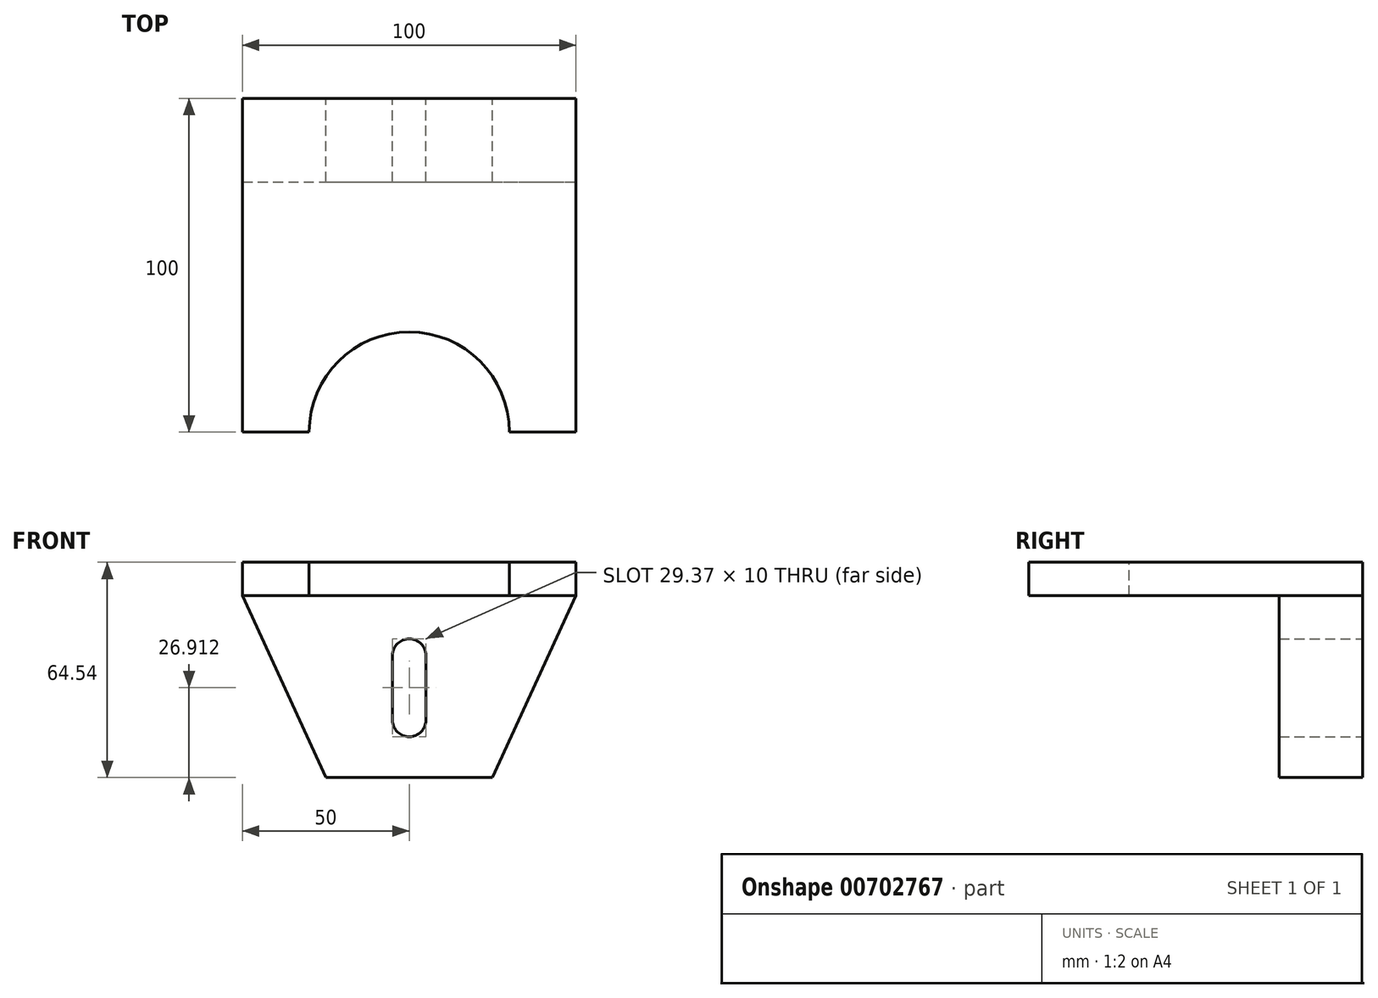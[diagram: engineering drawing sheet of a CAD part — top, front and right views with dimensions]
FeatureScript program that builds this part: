
annotation { "Feature Type Name" : "Feature", "Feature Type Description" : "" }
export const myFeature = defineFeature(function(context is Context, id is Id, definition is map)
    precondition{}
    {
        {
            var Q0;
            Q0=qCreatedBy(makeId("Front.planeOp"),FACE);
            var sketch = newSketch(context, id + "F0", { "sketchPlane" : qUnion([Q0])});
            skLineSegment(sketch, "E0", {"start": v(0, 0) * mm, "end": v(50, 0) * mm});
            skLineSegment(sketch, "E1", {"start": v(50, 0) * mm, "end": v(75, 54.54) * mm});
            skLineSegment(sketch, "E2", {"start": v(75, 54.54) * mm, "end": v(75, 64.54) * mm});
            skLineSegment(sketch, "E3", {"start": v(75, 64.54) * mm, "end": v(-25, 64.54) * mm});
            skLineSegment(sketch, "E4", {"start": v(-25, 64.54) * mm, "end": v(-25, 54.54) * mm});
            skLineSegment(sketch, "E5", {"start": v(-25, 54.54) * mm, "end": v(0, 0) * mm});
            skLineSegment(sketch, "E6", {"start": v(-25, 54.54) * mm, "end": v(75, 54.54) * mm});
            skSolve(sketch);
        }
        {
            var Q0;
            Q0=makeQuery(id+"F0.imprint","IMPRINT",FACE,{"disambiguationData":[TD([[makeQuery(id+"F0.imprint","IMPRINT",EDGE,{"derivedFrom":sQuery(id+"F0.wireOp",EDGE,"E2")}),1.0]])]});
            extrude(context, id + "F1", {"entities" : qUnion([Q0]), "depth" : 100 * mm, "offsetDistance" : 25 * mm});
        }
        {
            var Q0;
            Q0=makeQuery(id+"F0.imprint","IMPRINT",FACE,{"disambiguationData":[TD([[makeQuery(id+"F0.imprint","IMPRINT",EDGE,{"derivedFrom":sQuery(id+"F0.wireOp",EDGE,"E0")}),1.0]])]});
            extrude(context, id + "F2", {"entities" : qUnion([Q0]), "operationType" : NewBodyOperationType.ADD, "depth" : 25 * mm, "offsetDistance" : 25 * mm});
        }
        {
            var Q0;
            {var subQ0=sQuery(id+"F0.wireOp",EDGE,"E6");Q0=makeQuery(id+"F2.boolean.opBoolean","MERGE",FACE,{"derivedFrom":[makeQuery(id+"F1.opExtrude","CAP_FACE",FACE,{"disambiguationData":[OSD([sQuery(id+"F0.wireOp",EDGE,"E2"),sQuery(id+"F0.wireOp",EDGE,"E3"),sQuery(id+"F0.wireOp",EDGE,"E4"),subQ0])],"isStart":true}),makeQuery(id+"F2.opExtrude","CAP_FACE",FACE,{"disambiguationData":[OSD([sQuery(id+"F0.wireOp",EDGE,"E0"),sQuery(id+"F0.wireOp",EDGE,"E1"),sQuery(id+"F0.wireOp",EDGE,"E5"),subQ0])],"isStart":true})]});}
            var sketch = newSketch(context, id + "F3", { "sketchPlane" : qUnion([Q0])});
            skArc(sketch, "E7", {"start": v(-20, 36.6) * mm, "mid": v(-25, 41.6) * mm, "end": v(-30, 36.6) * mm});
            skPoint(sketch, "E7.centerSnap0", {"position": v(-25, 64.54) * mm});
            skArc(sketch, "E8", {"start": v(-30, 17.23) * mm, "mid": v(-25, 12.23) * mm, "end": v(-20, 17.23) * mm});
            skLineSegment(sketch, "E9", {"start": v(-30, 36.6) * mm, "end": v(-30, 17.23) * mm});
            skLineSegment(sketch, "E10", {"start": v(-20, 36.6) * mm, "end": v(-20, 17.23) * mm});
            skSolve(sketch);
        }
        {
            var Q0;
            Q0 = qSketchRegion(id + "F3", true);
            extrude(context, id + "F4", {"entities" : qUnion([Q0]), "operationType" : NewBodyOperationType.REMOVE, "oppositeDirection" : true, "depth" : 25 * mm, "offsetDistance" : 25 * mm});
        }
        {
            var Q0;
            Q0=makeQuery(id+"F1.opExtrude","SWEPT_FACE",FACE,{"disambiguationData":[OSD([sQuery(id+"F0.wireOp",EDGE,"E3")])]});
            var sketch = newSketch(context, id + "F5", { "sketchPlane" : qUnion([Q0])});
            skArc(sketch, "E11", {"start": v(55, -100) * mm, "mid": v(25, -70) * mm, "end": v(-5, -100) * mm});
            skSolve(sketch);
        }
        {
            var Q0;
            {var subQ0=sQuery(id+"F5.wireOp",EDGE,"E11");Q0=makeQuery(id+"F5.imprint","IMPRINT",FACE,{"disambiguationData":[TD([[makeQuery(id+"F5.imprint","IMPRINT",EDGE,{"derivedFrom":subQ0}),1.0]])]});}
            extrude(context, id + "F6", {"entities" : qUnion([Q0]), "operationType" : NewBodyOperationType.REMOVE, "oppositeDirection" : true, "depth" : 25 * mm, "offsetDistance" : 25 * mm});
        }
    });
